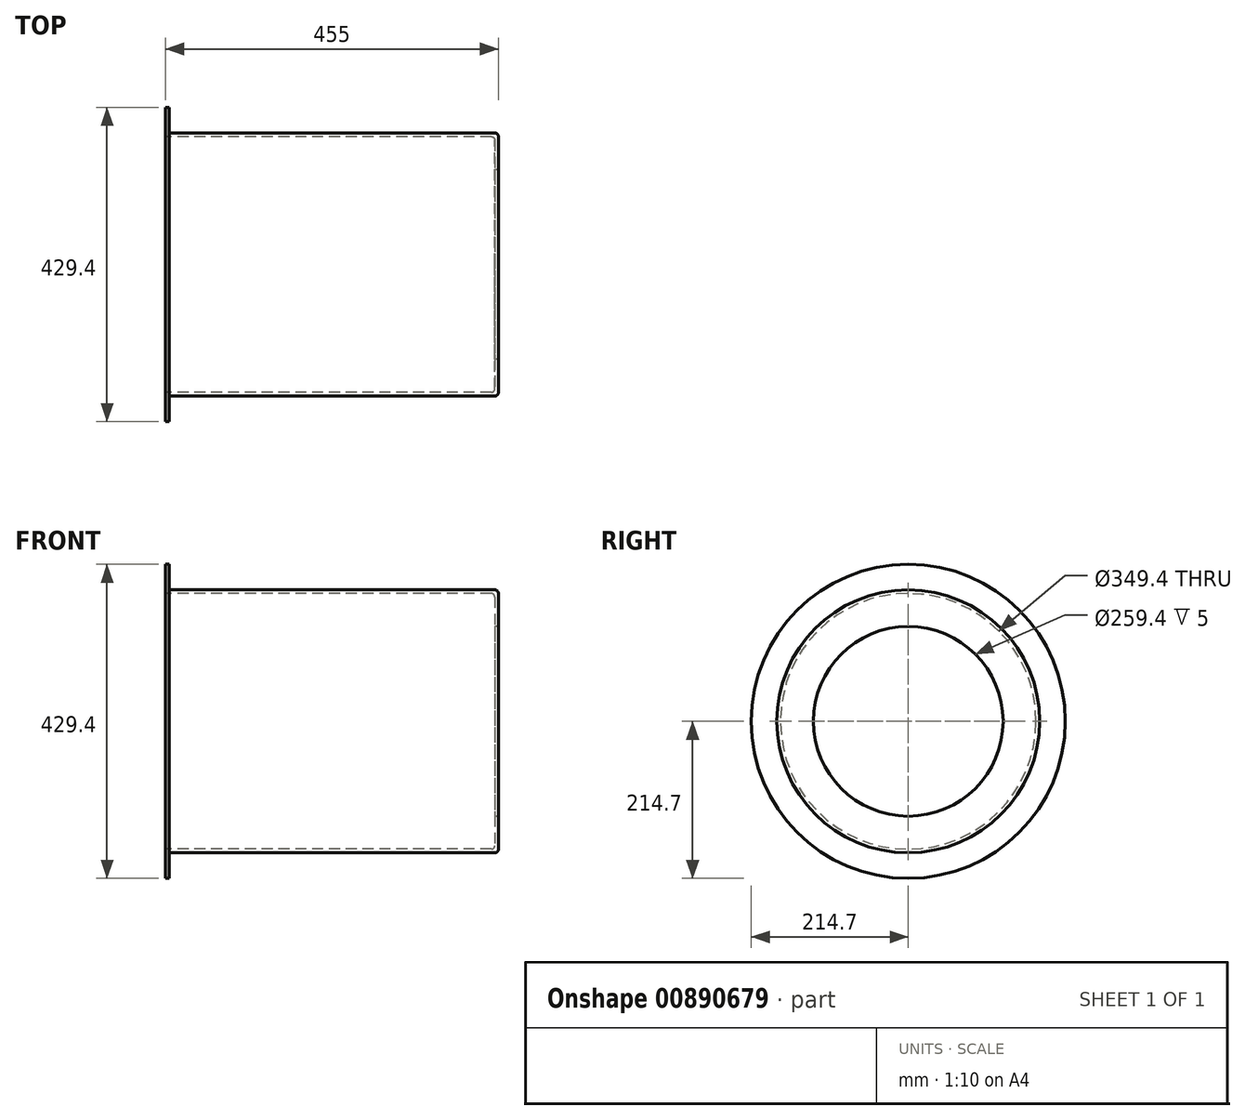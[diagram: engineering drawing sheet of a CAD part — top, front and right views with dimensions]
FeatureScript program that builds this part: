
annotation { "Feature Type Name" : "Feature", "Feature Type Description" : "" }
export const myFeature = defineFeature(function(context is Context, id is Id, definition is map)
    precondition{}
    {
        {
            var Q0;
            Q0=qCreatedBy(makeId("Front.planeOp"),FACE);
            var sketch = newSketch(context, id + "F0", { "sketchPlane" : qUnion([Q0])});
            skLineSegment(sketch, "E0", {"start": v(-42.2, 0) * mm, "end": v(60.23, 0) * mm, "construction": true});
            skLineSegment(sketch, "E1", {"start": v(-449, 179.7) * mm, "end": v(-5, 179.7) * mm});
            skLineSegment(sketch, "E2", {"start": v(0, 129.7) * mm, "end": v(0, 174.7) * mm});
            skLineSegment(sketch, "E3", {"start": v(-5, 129.7) * mm, "end": v(0, 129.7) * mm});
            skLineSegment(sketch, "E4", {"start": v(-450, 180.7) * mm, "end": v(-450, 214.7) * mm});
            skLineSegment(sketch, "E5", {"start": v(-450, 214.7) * mm, "end": v(-455, 214.7) * mm});
            skLineSegment(sketch, "E6", {"start": v(-455, 214.7) * mm, "end": v(-455, 176) * mm});
            skPoint(sketch, "E7.visualSharp", {"position": v(0, 179.7) * mm});
            skArc(sketch, "E7.filletArc", {"start": v(0, 174.7) * mm, "mid": v(-1.46, 178.24) * mm, "end": v(-5, 179.7) * mm});
            skPoint(sketch, "E8.visualSharp", {"position": v(-92.33, 120.18) * mm});
            skPoint(sketch, "E9.visualSharp", {"position": v(-450, 179.7) * mm});
            skArc(sketch, "E9.filletArc", {"start": v(-450, 180.7) * mm, "mid": v(-449.7, 180) * mm, "end": v(-449, 179.7) * mm});
            skPoint(sketch, "E10.visualSharp", {"position": v(-455, 25.85) * mm});
            skLineSegment(sketch, "E11", {"start": v(-453.7, 174.7) * mm, "end": v(-9.7, 174.7) * mm});
            skLineSegment(sketch, "E12", {"start": v(-5, 129.7) * mm, "end": v(-5, 170) * mm});
            skArc(sketch, "E13.filletArc", {"start": v(-5, 170) * mm, "mid": v(-6.38, 173.32) * mm, "end": v(-9.7, 174.7) * mm});
            skArc(sketch, "E14.filletArc", {"start": v(-455, 176) * mm, "mid": v(-454.62, 175.08) * mm, "end": v(-453.7, 174.7) * mm});
            skSolve(sketch);
        }
        {
            var Q0;
            Q0=makeQuery(id+"F0.imprint","IMPRINT",FACE,{"disambiguationData":[TD([[makeQuery(id+"F0.imprint","IMPRINT",EDGE,{"derivedFrom":sQuery(id+"F0.wireOp",EDGE,"E1")}),-1.0]])]});
            var Q1;
            Q1=sQuery(id+"F0.wireOp",EDGE,"E0");
            revolve(context, id + "F1", {"surfaceOperationType" : NewSurfaceOperationType.NEW, "entities" : qUnion([Q0]), "axis" : qUnion([Q1]), "revolveType" : RevolveType.FULL});
        }
    });
